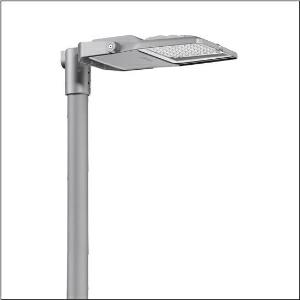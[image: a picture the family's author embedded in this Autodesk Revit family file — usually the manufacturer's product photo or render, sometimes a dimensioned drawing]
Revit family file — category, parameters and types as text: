
# Revit family: floodlight_fl_21_iq_mini___pl52_5xa7771d4d3a_bc98
name_source: partatom
category: Lighting Fixtures
units: mm (PartAtom-declared; Revit-internal decimal feet)

## family parameters
Cut with Voids When Loaded = No
Host = Face
Light Source = No
Part Type = Normal
Room Calculation Point = No
Round Connector Dimension = Use Diameter
Shared = No

## types (1)
- --- (1 x LED, 18610 lm, 143 W, 4000K)
    Apparent Load = 143 VA
    CIE Flux Codes = 26 60 98 100 100
    Color Rendering = 70
    Color Temperature = 4000K
    Default Elevation = 1800 mm
    Description = Floodlight FL 21 iQ mini, floodlight, primary light control with lens, of PMMA, primary optical cover: protective disc, of toughened safety glass, transparent, light distribution: PL52, light emission: direct distribution, installation type: surface-mounted, LED, High Power LED, rated luminous flux: 18.610lm, luminous efficacy: 130lm/W, light colour: 740, colour temperature: 4000K, control: Auto-Match, Temp-Guard, Lumen-Switch, Night-Set, Smart-Wire, Light-Fading, Desk-Remote (wireless, voltage-free reading and setting of iQ features in the workshop via application-optimized NFC function/RFID function), optimised constant luminous flux control (CLO 2.0), with terminal, 6-pole, mains connection: 220..240V, AC, 50/60Hz, start of lifetime: 143W, end of service life: 152W, reduction: 61W, luminaire housing, of diecast aluminium, powder-coated, Siteco® metallic grey (DB 702S), corrosivity category C5 mid according to DIN EN ISO 12944, sealing non-destructively replaceable, please order mast flange separately, mast bracket, of steel, galvanised, powder-coated, Siteco® metallic grey (DB 702S), protection rating (complete): IP66, insulation class (complete): insulation class II (safety insulation), certification: CE, ENEC, VDE, protection symbol: D, impact resistance: IK08, permissible operating ambient temperature: -40..+40°C, permissible operating ambient temperature for outdoor applications: -40..+50°C, standard: DIN EN 12944, LABS conformity tested according to VDMA 24364:2018-05, packaging unit: 1 piece

Light Distribution: PL52
    Height = 70 mm
    Lamp = 1 x LED
    Lamp Light Flux = 18610 lm
    Lamp Power = 143 W
    Lamp count = 1
    Length = 485 mm
    Luminous efficacy = 130 lm/W
    Manufacturer = Siteco
    ModVariant = No
    Model = 5XA7771D4D3A
    Number of Poles = 1
    OnlyDefault = Yes
    Power Factor = 1
    Product Name = Floodlight FL 21 iQ mini | PL52
    Product group = floodlight | pylon annexe
    ProductGroupID = 6200
    Protection Class = Protection class II
    Protection Degree = IP 66
    RLX_Detail_Level = 1
    RLX_Emergency_Light_Flux = 0 lm
    RLX_Emergency_Type = 0
    RLX_Emergency_Type_DB = No
    RlxData = <blob elided: 101749 chars, md5=22465869>
    Socket = socket
    Standby Power = 0 W
    System Light Flux = 18610 lm
    System Power = 143 W
    Type Comments = factory setting: luminous flux: 100 % | dim-lin: 254 | 730 mA
    Type Image = l_1007125.jpg
    URL = http://relux.com
    VarID = @adj_134197
    Voltage = 0 V
    Weight = 0.00 kg
    Width = 337 mm

## geometry (parser evidence)
native form markers: Blend x4, Sweep x12
no freeform markers — native parametric forms only
